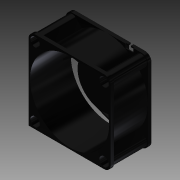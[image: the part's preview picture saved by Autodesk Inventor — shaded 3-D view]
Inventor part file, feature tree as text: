
AUTODESK INVENTOR PART (.ipt)
format: ipt  version: 2014 SP1 (Build 180222100, 222)  size: 281,088 bytes
history: native  units: mm (DEFAULTED — no unit token found)
features: sketch x10, extrude x9, plane x1, revolve x1, fillet x1, pattern_circular x1, other x1, projected_geometry x1
ambient origin geometry x8: Origin, YZ Plane, XZ Plane, XY Plane, X Axis, Y Axis, Z Axis, Center Point
bodies: Solid1 (feature_tree)
feature tree (25):
  extrude  "Extrusion1"  Depth=39.878mm
  plane  "Work Plane1"
  revolve  "Revolution1"  [1 undecoded]
  fillet  "Fillet1"  Radius=1.7018mm
  extrude  "Extrusion2"  TaperAngle=90.0deg  [1 undecoded]
  extrude  "Extrusion3"  Depth=3.175mm
  pattern_circular  "Circular Pattern1"  Count=4 Angle=360.0deg
  extrude  "Extrusion4"  Depth=19.812mm
  extrude  "fan support1"  Depth=0.635mm
  extrude  "fan support2"  Depth=3.81mm TaperAngle=0.0deg
  extrude  "fan support3"  Depth=8.001mm
  extrude  "fan support4"  Depth=1.5875mm
  extrude  "fan support5"  Depth=1.5875mm TaperAngle=0.0deg
  other  "fan interface"
  sketch  "Sketch1"  dims[d0=39.878mm d1=39.878mm]
  sketch  "Sketch2"  dims[d2=19.812mm d3=0.0mm d4=1.7018mm d5=1.7018mm]
  sketch  "Sketch3"  dims[d6=12.7mm d7=90.0deg]
  sketch  "Sketch4"  dims[d8=3.175mm d9=4.572mm]
  sketch  "Sketch5"  dims[d10=19.812mm d11=0.0mm]
  projected_geometry  "Projected Loop1"
  sketch  "Sketch6"  dims[d12=19.812mm d13=0.0mm d14=40.0mm d16=360.0deg]
  sketch  "Sketch7"  dims[d17=19.812mm d18=0.0mm d19=38.481mm]
  sketch  "Sketch8"  dims[d20=24.2824mm d21=0.635mm]
  sketch  "Sketch9"  dims[d23=0.635mm d24=3.81mm d25=0.0mm]
  sketch  "Sketch10"  dims[d26=5.08mm d27=8.001mm d28=4.0005mm d29=1.5875mm d30=0.0mm d31=22.896572mm d32=0.635mm d33=0.635mm d34=0.635mm d35=0.635mm d36=1.27mm d37=0.0mm d38=1.55575mm d39=0.0mm d40=1.55575mm d41=0.0mm d42=1.5875mm]
note: 2 required parameter values undecoded (feature->parameter linkage not recoverable at this tier; creation-order binding heuristic only, values carry confidence <= 0.55)